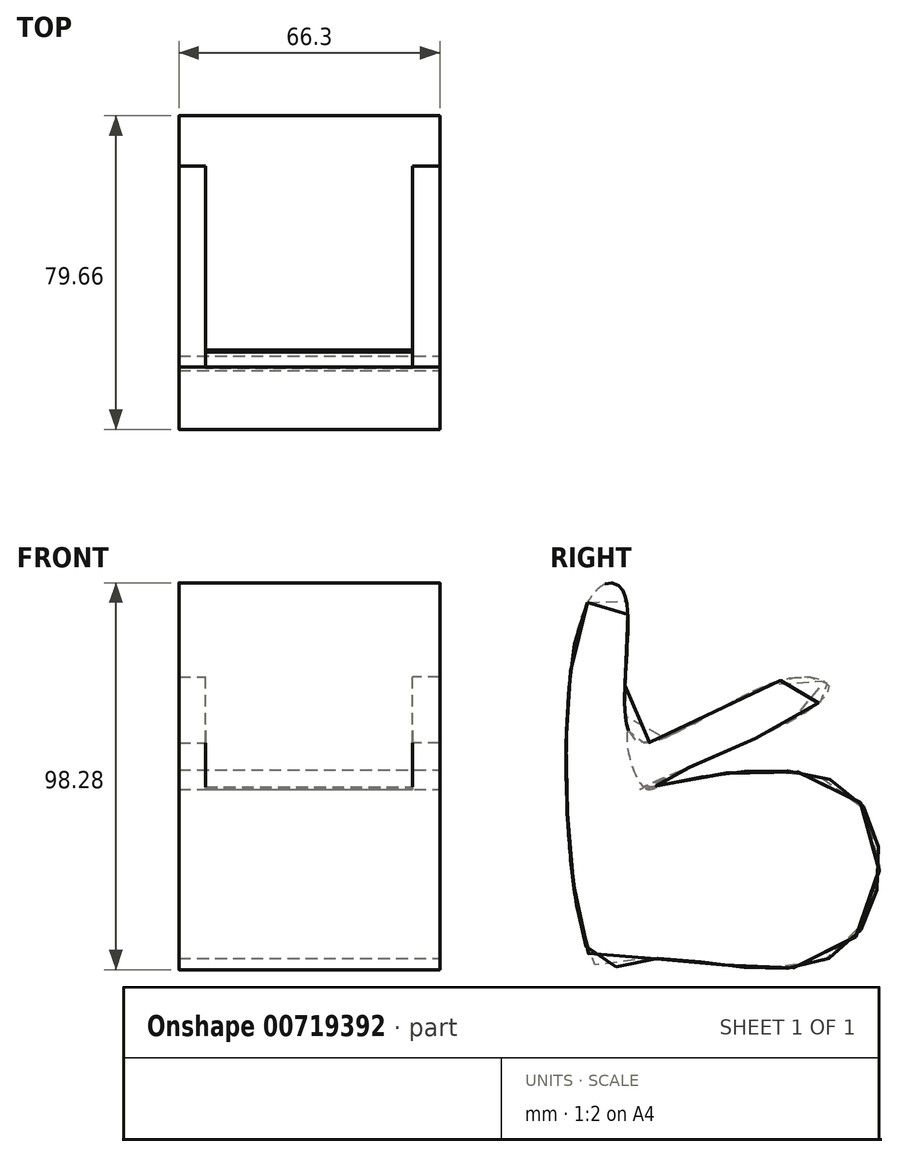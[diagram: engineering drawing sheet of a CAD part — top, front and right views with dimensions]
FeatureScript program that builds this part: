
annotation { "Feature Type Name" : "Feature", "Feature Type Description" : "" }
export const myFeature = defineFeature(function(context is Context, id is Id, definition is map)
    precondition{}
    {
        {
            var Q0;
            Q0=qCreatedBy(makeId("Right.planeOp"),FACE);
            var sketch = newSketch(context, id + "F0", { "sketchPlane" : qUnion([Q0])});
            skFitSpline(sketch, "E0", {"points": [v(-34.16, 39.42) * mm, v(-25.03, 42.18) * mm, v(-22.54, 4.84) * mm, v(15.35, 19.78) * mm, v(26.77, 16.3) * mm, v(-21, -7.89) * mm, v(29.46, -6.5) * mm, v(30.29, -49.1) * mm, v(-20.81, -51.18) * mm, v(-32.5, -52.42) * mm, v(-34.16, 39.42) * mm]});
            skSolve(sketch);
        }
        {
            var Q0;
            Q0=makeQuery(id+"F0.imprint","IMPRINT",FACE,{"disambiguationData":[TD([[makeQuery(id+"F0.imprint","IMPRINT",EDGE,{"derivedFrom":sQuery(id+"F0.wireOp",EDGE,"E0")}),-1.0]])]});
            extrude(context, id + "F1", {"entities" : qUnion([Q0]), "depth" : 66.3 * mm, "offsetDistance" : 25 * mm});
        }
        {
            var Q0;
            Q0=qCreatedBy(makeId("Right.planeOp"),FACE);
            cPlane(context, id + "F2", {"entities" : qUnion([Q0]), "cplaneType" : CPlaneType.OFFSET, "offset" : 59.3 * mm, "width" : 150 * mm, "height" : 150 * mm});
        }
        {
            var Q0;
            Q0=qCreatedBy(id+"F2.planeOp",FACE);
            var sketch = newSketch(context, id + "F3", { "sketchPlane" : qUnion([Q0])});
            skFitSpline(sketch, "E1", {"points": [v(-23.93, 6.78) * mm, v(-19.78, -7.6) * mm, v(-13.42, -5.4) * mm, v(5.4, 0) * mm, v(30.84, 16.74) * mm, v(21.71, 21.71) * mm, v(0, 14.52) * mm, v(-18.67, 6.78) * mm, v(-23.93, 6.78) * mm]});
            skSolve(sketch);
        }
        {
            var Q0;
            Q0 = qSketchRegion(id + "F3", true);
            extrude(context, id + "F4", {"entities" : qUnion([Q0]), "operationType" : NewBodyOperationType.REMOVE, "oppositeDirection" : true, "depth" : 52.5 * mm, "offsetDistance" : 25 * mm});
        }
        {
            var Q0;
            Q0=makeQuery(id+"F4.boolean.opBoolean","INTERSECT",EDGE,{"disambiguationData":[OD(2.0)],"derivedFrom":[makeQuery(id+"F1.opExtrude","SWEPT_FACE",FACE,{"disambiguationData":[OSD([sQuery(id+"F0.wireOp",EDGE,"E0")])]}),makeQuery(id+"F4.opExtrude","SWEPT_FACE",FACE,{"disambiguationData":[OSD([sQuery(id+"F3.wireOp",EDGE,"E1")])]})]});
            var Q1;
            Q1=makeQuery(id+"F1.opExtrude","CAP_FACE",FACE,{"disambiguationData":[OSD([sQuery(id+"F0.wireOp",EDGE,"E0")])],"isStart":false});
            var Q2;
            Q2=makeQuery(id+"F1.opExtrude","CAP_EDGE",EDGE,{"disambiguationData":[OSD([sQuery(id+"F0.wireOp",EDGE,"E0")])],"isStart":true});
            var Q3;
            Q3=makeQuery(id+"F4.boolean.opBoolean","INTERSECT",EDGE,{"disambiguationData":[OD(3.0)],"derivedFrom":[makeQuery(id+"F1.opExtrude","SWEPT_FACE",FACE,{"disambiguationData":[OSD([sQuery(id+"F0.wireOp",EDGE,"E0")])]}),makeQuery(id+"F4.opExtrude","SWEPT_FACE",FACE,{"disambiguationData":[OSD([sQuery(id+"F3.wireOp",EDGE,"E1")])]})]});
            fillet(context, id + "F5", {"entities" : qUnion([Q0, Q1, Q2, Q3]), "radius" : 0.01 * mm, "tangentPropagation" : true, "allowEdgeOverflow" : false});
        }
    });
